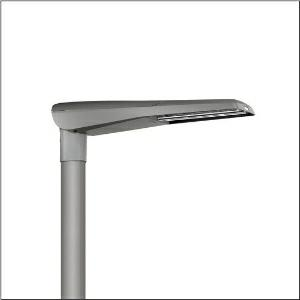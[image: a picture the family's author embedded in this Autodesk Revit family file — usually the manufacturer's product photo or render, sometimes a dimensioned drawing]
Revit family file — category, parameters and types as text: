
# Revit family: streetlight_sl_11_iq_mini___st1_2a_5xc2ac1f08ge_c732
name_source: partatom
category: Lighting Fixtures
units: mm (PartAtom-declared; Revit-internal decimal feet)

## family parameters
Cut with Voids When Loaded = No
Host = Face
Light Source = No
Part Type = Normal
Room Calculation Point = No
Round Connector Dimension = Use Diameter
Shared = No

## types (1)
- --- (1 x LED, 3040 lm, 25.3 W, 2200K)
    Apparent Load = 25 VA
    CIE Flux Codes = 32 70 96 100 100
    Color Rendering = 70
    Color Temperature = 2200K
    Default Elevation = 1800 mm
    Description = Streetlight SL 11 iQ mini, mast luminaire, primary light control with 3 zone facetted reflector, of plastic, silver coated, highly specular, primary optical cover: cover, of PMMA, transparent, light distribution: ST1.2a, light emission: direct distribution, primary light characteristic: asymmetric, installation type: post-top, side-entry, lamps: LED, High Power LED, rated values: 3.570lm | 24,9W | 143,4lm/W (begin service life); end service life: 3.570lm | 25,7W; at 50% lumin. flux: 1.785lm | 12,8W | 139,5lm/W, colour temperature: 2200/2700/3000/4000K, colour rendering: CRI > 70, light colour: 722/727/730/740, light setting 1 begin service life: 100% | 3.570lm | 24,9W | 143,4lm/W | 3.000K, light setting 1 end service life: 25,7W, further light settings possible, control: Street-Remote, Auto-Match, Temp-Guard, Lumen-Switch, Night-Set, Smart-Wire, Light-Fading, Desk-Remote (wireless, voltage-free reading and setting of iQ features in the workshop via application-optimized NFC function/RFID function), optimised constant luminous flux control (CLO 2.0), with cable H07RN-F 5x 1.5mm², mains connection: 230..240V, AC, 50/60Hz, connection cable pre-assembled, cable length: 6,5m, luminaire housing, of diecast aluminium, powder-coated, Siteco® metallic grey (DB 702S), please order mast flange separately, inclination adjustable without tools: 0°, 5°, 10°, 15° (post-top) | 0°, -5°, -10°, -15° (side-entry), sealing non-destructively replaceable, multi-level sealing system, length: 736mm, width: 174mm, height: 116mm, mast flange for spigot size: 42mm (side-entry): 5XC10008XM4, 60/48mm (side-entry/post-top): 5XC10108XM2, 76/60mm (side-entry/post-top): 5XC10108XM1, equipment: standard, protection rating (complete): IP66, insulation class (complete): insulation class II (safety insulation), certification: CE, ENEC, ENEC+, VDE, impact resistance: IK10, permissible operating ambient temperature for outdoor applications: -25..+50°C, standard-compliant lighting for roads and squares, Environmental Product Declaration (EPD) tested and certified by an independent institute, packaging unit: 1 piece

Light Distribution: ST1.2a
    Height = 116 mm
    Lamp = 1 x LED
    Lamp Light Flux = 3040 lm
    Lamp Power = 25.3 W
    Lamp count = 1
    Length = 736 mm
    Luminous efficacy = 120 lm/W
    Manufacturer = Siteco
    ModVariant = No
    Model = 5XC2AC1F08GE
    Number of Poles = 1
    OnlyDefault = Yes
    Power Factor = 1
    Product Name = Streetlight SL 11 iQ mini | ST1.2a
    Product group = mast luminaire | pylon top
    ProductGroupID = 6100
    Protection Class = Protection class II
    Protection Degree = IP 66
    RLX_Detail_Level = 1
    RLX_Emergency_Light_Flux = 0 lm
    RLX_Emergency_Type = 0
    RLX_Emergency_Type_DB = No
    RlxData = <blob elided: 53537 chars, md5=0480c7e7>
    Socket = socket
    Standby Power = 0 W
    System Light Flux = 3040 lm
    System Power = 25 W
    Type Comments = individual setting: luminous flux: 100 % | dim-lin: 254 | 351 mA
    Type Image = l_1003508.jpg
    URL = http://relux.com
    VarID = @adj_035110
    Voltage = 0 V
    Weight = 0.00 kg
    Width = 174 mm

## geometry (parser evidence)
native form markers: Blend x4, Sweep x10
no freeform markers — native parametric forms only
